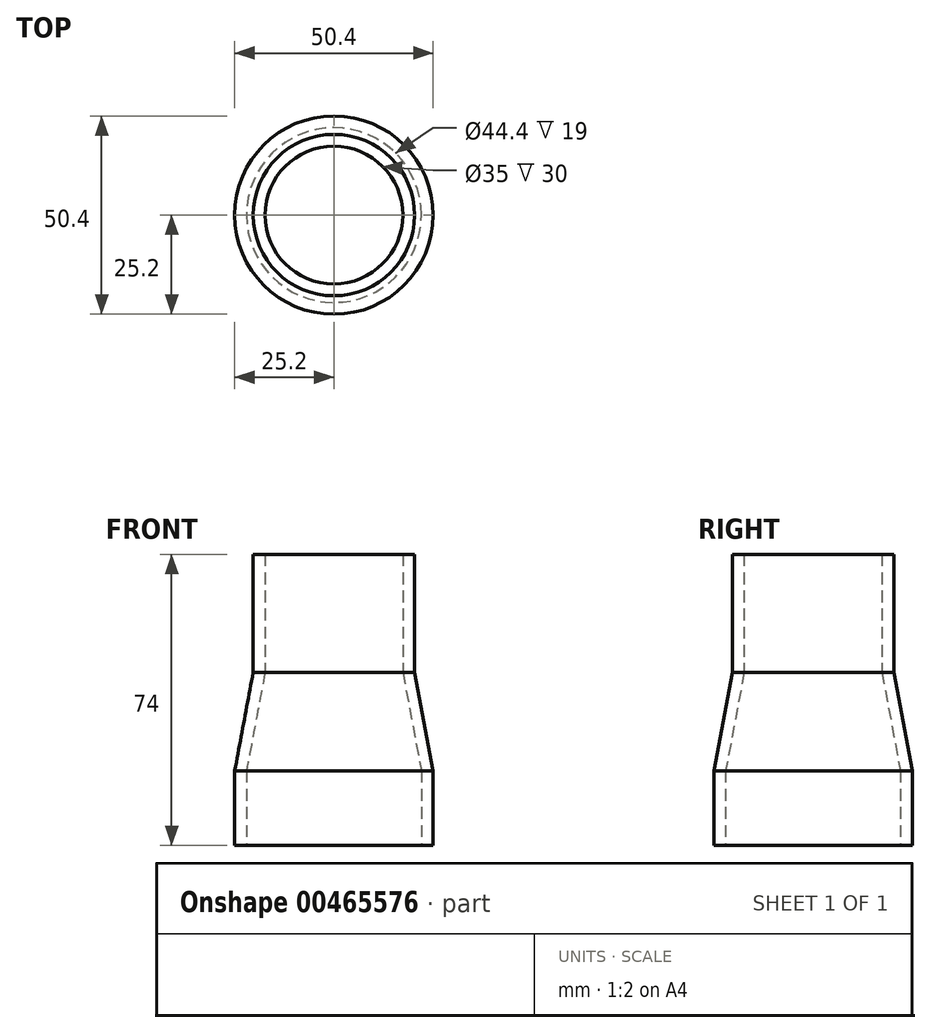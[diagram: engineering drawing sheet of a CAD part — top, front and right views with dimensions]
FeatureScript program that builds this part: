
annotation { "Feature Type Name" : "Feature", "Feature Type Description" : "" }
export const myFeature = defineFeature(function(context is Context, id is Id, definition is map)
    precondition{}
    {
        {
            var Q0;
            Q0=qCreatedBy(makeId("Front.planeOp"),FACE);
            var sketch = newSketch(context, id + "F0", { "sketchPlane" : qUnion([Q0])});
            skLineSegment(sketch, "E0", {"start": v(-20.5, 25) * mm, "end": v(-20.5, 55) * mm});
            skLineSegment(sketch, "E1", {"start": v(-20.5, 25) * mm, "end": v(-25.2, 0) * mm});
            skLineSegment(sketch, "E2", {"start": v(-20.5, 55) * mm, "end": v(-17.5, 55) * mm});
            skLineSegment(sketch, "E3", {"start": v(-17.5, 55) * mm, "end": v(-17.5, 25) * mm});
            skLineSegment(sketch, "E4", {"start": v(-17.5, 25) * mm, "end": v(-22.2, 0) * mm});
            skLineSegment(sketch, "E5", {"start": v(0, 0) * mm, "end": v(0, 66.57) * mm, "construction": true});
            skLineSegment(sketch, "E6", {"start": v(-22.2, 0) * mm, "end": v(-22.2, -19) * mm});
            skLineSegment(sketch, "E7", {"start": v(-22.2, -19) * mm, "end": v(-25.2, -19) * mm});
            skLineSegment(sketch, "E8", {"start": v(-25.2, -19) * mm, "end": v(-25.2, 0) * mm});
            skSolve(sketch);
        }
        {
            var Q0;
            Q0=makeQuery(id+"F0.imprint","IMPRINT",FACE,{"disambiguationData":[TD([[makeQuery(id+"F0.imprint","IMPRINT",EDGE,{"derivedFrom":sQuery(id+"F0.wireOp",EDGE,"E0")}),-1.0]])]});
            var Q1;
            Q1=sQuery(id+"F0.wireOp",EDGE,"E5");
            revolve(context, id + "F1", {"surfaceOperationType" : NewSurfaceOperationType.NEW, "entities" : qUnion([Q0]), "axis" : qUnion([Q1]), "revolveType" : RevolveType.FULL});
        }
    });
